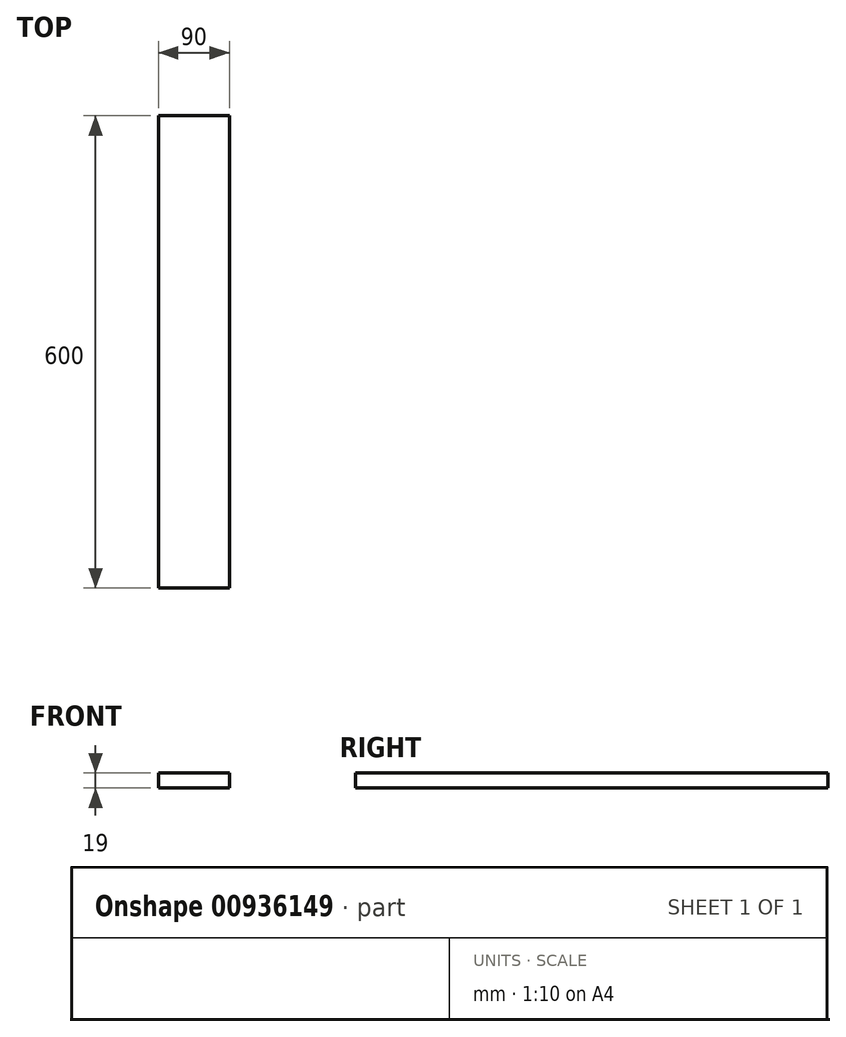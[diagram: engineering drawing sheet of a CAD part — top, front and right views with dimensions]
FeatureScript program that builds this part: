
annotation { "Feature Type Name" : "Feature", "Feature Type Description" : "" }
export const myFeature = defineFeature(function(context is Context, id is Id, definition is map)
    precondition{}
    {
        {
            var Q0;
            Q0=qCreatedBy(makeId("Front.planeOp"),FACE);
            var sketch = newSketch(context, id + "F0", { "sketchPlane" : qUnion([Q0])});
            skLineSegment(sketch, "E0.bottom", {"start": v(0, 0) * mm, "end": v(90, 0) * mm});
            skLineSegment(sketch, "E0.top", {"start": v(0, 19) * mm, "end": v(90, 19) * mm});
            skLineSegment(sketch, "E0.left", {"start": v(0, 0) * mm, "end": v(0, 19) * mm});
            skLineSegment(sketch, "E0.right", {"start": v(90, 0) * mm, "end": v(90, 19) * mm});
            skSolve(sketch);
        }
        {
            var Q0;
            Q0=makeQuery(id+"F0.imprint","IMPRINT",FACE,{"disambiguationData":[TD([[makeQuery(id+"F0.imprint","IMPRINT",EDGE,{"derivedFrom":sQuery(id+"F0.wireOp",EDGE,"E0.bottom")}),1.0]])]});
            extrude(context, id + "F1", {"entities" : qUnion([Q0]), "depth" : 600 * mm, "offsetDistance" : 25 * mm});
        }
    });
